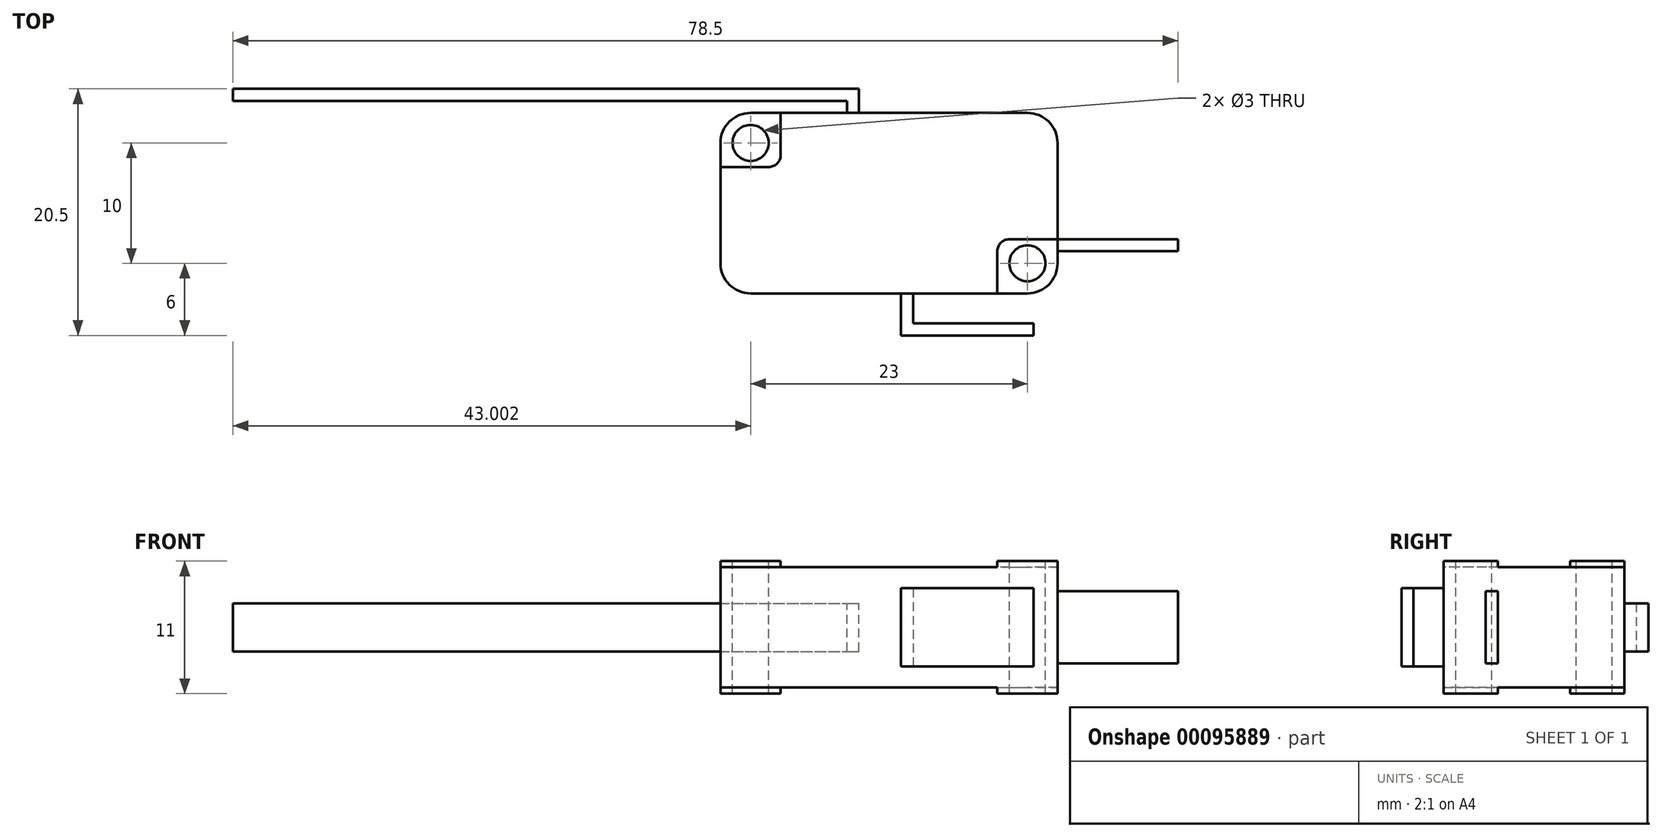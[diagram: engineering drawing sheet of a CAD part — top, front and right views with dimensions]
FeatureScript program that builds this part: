
annotation { "Feature Type Name" : "Feature", "Feature Type Description" : "" }
export const myFeature = defineFeature(function(context is Context, id is Id, definition is map)
    precondition{}
    {
        {
            var Q0;
            Q0=qCreatedBy(makeId("Top.planeOp"),FACE);
            var sketch = newSketch(context, id + "F0", { "sketchPlane" : qUnion([Q0])});
            skLineSegment(sketch, "E0.bottom", {"start": v(-11.85, 4.57) * mm, "end": v(11.15, 4.57) * mm});
            skLineSegment(sketch, "E0.top", {"start": v(-11.85, -10.43) * mm, "end": v(11.15, -10.43) * mm});
            skLineSegment(sketch, "E0.left", {"start": v(-14.35, 2.07) * mm, "end": v(-14.35, -7.93) * mm});
            skLineSegment(sketch, "E0.right", {"start": v(13.65, 2.07) * mm, "end": v(13.65, -7.93) * mm});
            skPoint(sketch, "E1.visualSharp", {"position": v(-14.35, 4.57) * mm});
            skArc(sketch, "E1.filletArc", {"start": v(-11.85, 4.57) * mm, "mid": v(-13.62, 3.84) * mm, "end": v(-14.35, 2.07) * mm});
            skPoint(sketch, "E2.visualSharp", {"position": v(13.65, 4.57) * mm});
            skArc(sketch, "E2.filletArc", {"start": v(13.65, 2.07) * mm, "mid": v(12.92, 3.84) * mm, "end": v(11.15, 4.57) * mm});
            skPoint(sketch, "E3.visualSharp", {"position": v(13.65, -10.43) * mm});
            skArc(sketch, "E3.filletArc", {"start": v(11.15, -10.43) * mm, "mid": v(12.92, -9.7) * mm, "end": v(13.65, -7.93) * mm});
            skPoint(sketch, "E4.visualSharp", {"position": v(-14.35, -10.43) * mm});
            skArc(sketch, "E4.filletArc", {"start": v(-14.35, -7.93) * mm, "mid": v(-13.62, -9.7) * mm, "end": v(-11.85, -10.43) * mm});
            skSolve(sketch);
        }
        {
            var Q0;
            Q0=qSketchRegion(id+"F0",true);
            extrude(context, id + "F1", {"entities" : qUnion([Q0]), "depth" : 10 * mm});
        }
        {
            var Q0;
            Q0=makeQuery(id+"F1.opExtrude","CAP_FACE",FACE,{"disambiguationData":[OSD([sQuery(id+"F0.wireOp",EDGE,"E0.bottom"),sQuery(id+"F0.wireOp",EDGE,"E0.top"),sQuery(id+"F0.wireOp",EDGE,"E0.left"),sQuery(id+"F0.wireOp",EDGE,"E0.right"),sQuery(id+"F0.wireOp",EDGE,"E1.filletArc"),sQuery(id+"F0.wireOp",EDGE,"E2.filletArc"),sQuery(id+"F0.wireOp",EDGE,"E3.filletArc"),sQuery(id+"F0.wireOp",EDGE,"E4.filletArc")])],"isStart":false});
            var sketch = newSketch(context, id + "F2", { "sketchPlane" : qUnion([Q0])});
            skCircle(sketch, "E5", {"center": v(-11.85, 2.07) * mm, "radius": 1.5 * mm});
            skCircle(sketch, "E6", {"center": v(11.15, -7.93) * mm, "radius": 1.5 * mm});
            skSolve(sketch);
        }
        {
            var Q0;
            Q0=qSketchRegion(id+"F2",true);
            extrude(context, id + "F3", {"entities" : qUnion([Q0]), "operationType" : NewBodyOperationType.REMOVE, "oppositeDirection" : true, "depth" : 15 * mm});
        }
        {
            var Q0;
            Q0=makeQuery(id+"F1.opExtrude","CAP_FACE",FACE,{"disambiguationData":[OSD([sQuery(id+"F0.wireOp",EDGE,"E0.bottom"),sQuery(id+"F0.wireOp",EDGE,"E0.top"),sQuery(id+"F0.wireOp",EDGE,"E0.left"),sQuery(id+"F0.wireOp",EDGE,"E0.right"),sQuery(id+"F0.wireOp",EDGE,"E1.filletArc"),sQuery(id+"F0.wireOp",EDGE,"E2.filletArc"),sQuery(id+"F0.wireOp",EDGE,"E3.filletArc"),sQuery(id+"F0.wireOp",EDGE,"E4.filletArc")])],"isStart":false});
            var sketch = newSketch(context, id + "F4", { "sketchPlane" : qUnion([Q0])});
            skPoint(sketch, "E7", {"position": v(-9.35, 4.57) * mm});
            skPoint(sketch, "E8", {"position": v(-9.35, 0.07) * mm});
            skLineSegment(sketch, "E9.bottom", {"start": v(-9.35, 4.57) * mm, "end": v(-14.35, 4.57) * mm});
            skLineSegment(sketch, "E9.top", {"start": v(-10.35, 0.07) * mm, "end": v(-14.35, 0.07) * mm});
            skLineSegment(sketch, "E9.left", {"start": v(-9.35, 4.57) * mm, "end": v(-9.35, 1.07) * mm});
            skLineSegment(sketch, "E9.right", {"start": v(-14.35, 4.57) * mm, "end": v(-14.35, 0.07) * mm});
            skPoint(sketch, "E10", {"position": v(8.65, -10.43) * mm});
            skPoint(sketch, "E11", {"position": v(8.65, -5.93) * mm});
            skLineSegment(sketch, "E12.bottom", {"start": v(9.65, -5.93) * mm, "end": v(13.66, -5.93) * mm});
            skLineSegment(sketch, "E12.top", {"start": v(8.65, -10.43) * mm, "end": v(13.66, -10.43) * mm});
            skLineSegment(sketch, "E12.left", {"start": v(8.65, -6.93) * mm, "end": v(8.65, -10.43) * mm});
            skLineSegment(sketch, "E12.right", {"start": v(13.66, -5.93) * mm, "end": v(13.66, -10.43) * mm});
            skArc(sketch, "E13.filletArc", {"start": v(9.65, -5.93) * mm, "mid": v(8.95, -6.22) * mm, "end": v(8.65, -6.93) * mm});
            skArc(sketch, "E14.filletArc", {"start": v(-10.35, 0.07) * mm, "mid": v(-9.64, 0.36) * mm, "end": v(-9.35, 1.07) * mm});
            skSolve(sketch);
        }
        {
            var Q0;
            {var subQ3=sQuery(id+"F4.wireOp",EDGE,"E9.top");Q0=makeQuery(id+"F4.imprint","IMPRINT",FACE,{"disambiguationData":[TD([[makeQuery(id+"F4.imprint","IMPRINT",EDGE,{"derivedFrom":subQ3}),-1.0]])]});}
            var Q1;
            {var subQ3=sQuery(id+"F4.wireOp",EDGE,"E12.left");Q1=makeQuery(id+"F4.imprint","IMPRINT",FACE,{"disambiguationData":[TD([[makeQuery(id+"F4.imprint","IMPRINT",EDGE,{"derivedFrom":subQ3}),1.0]])]});}
            extrude(context, id + "F5", {"entities" : qUnion([Q0, Q1]), "operationType" : NewBodyOperationType.ADD, "depth" : 0.5 * mm});
        }
        {
            var Q0;
            Q0=makeQuery(id+"F1.opExtrude","CAP_FACE",FACE,{"disambiguationData":[OSD([sQuery(id+"F0.wireOp",EDGE,"E0.bottom"),sQuery(id+"F0.wireOp",EDGE,"E0.top"),sQuery(id+"F0.wireOp",EDGE,"E0.left"),sQuery(id+"F0.wireOp",EDGE,"E0.right"),sQuery(id+"F0.wireOp",EDGE,"E1.filletArc"),sQuery(id+"F0.wireOp",EDGE,"E2.filletArc"),sQuery(id+"F0.wireOp",EDGE,"E3.filletArc"),sQuery(id+"F0.wireOp",EDGE,"E4.filletArc")])],"isStart":true});
            var sketch = newSketch(context, id + "F6", { "sketchPlane" : qUnion([Q0])});
            skLineSegment(sketch, "E15.bottom", {"start": v(-14.35, -0.07) * mm, "end": v(-10.35, -0.07) * mm});
            skLineSegment(sketch, "E15.top", {"start": v(-14.35, -4.57) * mm, "end": v(-9.35, -4.57) * mm});
            skLineSegment(sketch, "E15.left", {"start": v(-14.35, -0.07) * mm, "end": v(-14.35, -4.57) * mm});
            skLineSegment(sketch, "E15.right", {"start": v(-9.35, -1.07) * mm, "end": v(-9.35, -4.57) * mm});
            skLineSegment(sketch, "E16.bottom", {"start": v(8.65, 10.43) * mm, "end": v(13.65, 10.43) * mm});
            skLineSegment(sketch, "E16.top", {"start": v(9.65, 5.93) * mm, "end": v(13.65, 5.93) * mm});
            skLineSegment(sketch, "E16.left", {"start": v(8.65, 10.43) * mm, "end": v(8.65, 6.93) * mm});
            skLineSegment(sketch, "E16.right", {"start": v(13.65, 10.43) * mm, "end": v(13.65, 5.93) * mm});
            skPoint(sketch, "E17.visualSharp", {"position": v(8.65, 5.93) * mm});
            skArc(sketch, "E17.filletArc", {"start": v(8.65, 6.93) * mm, "mid": v(8.95, 6.22) * mm, "end": v(9.65, 5.93) * mm});
            skPoint(sketch, "E18.visualSharp", {"position": v(-9.35, -0.07) * mm});
            skArc(sketch, "E18.filletArc", {"start": v(-9.35, -1.07) * mm, "mid": v(-9.64, -0.36) * mm, "end": v(-10.35, -0.07) * mm});
            skSolve(sketch);
        }
        {
            var Q0;
            {var subQ3=sQuery(id+"F6.wireOp",EDGE,"E15.bottom");Q0=makeQuery(id+"F6.imprint","IMPRINT",FACE,{"disambiguationData":[TD([[makeQuery(id+"F6.imprint","IMPRINT",EDGE,{"derivedFrom":subQ3}),-1.0]])]});}
            var Q1;
            {var subQ3=sQuery(id+"F6.wireOp",EDGE,"E16.top");Q1=makeQuery(id+"F6.imprint","IMPRINT",FACE,{"disambiguationData":[TD([[makeQuery(id+"F6.imprint","IMPRINT",EDGE,{"derivedFrom":subQ3}),1.0]])]});}
            extrude(context, id + "F7", {"entities" : qUnion([Q0, Q1]), "operationType" : NewBodyOperationType.ADD, "depth" : 0.5 * mm});
        }
        {
            var Q0;
            {var subQ0=sQuery(id+"F0.wireOp",EDGE,"E0.right");Q0=makeQuery(id+"F7.boolean.opBoolean","MERGE",FACE,{"derivedFrom":[makeQuery(id+"F5.boolean.opBoolean","MERGE",FACE,{"derivedFrom":[makeQuery(id+"F1.opExtrude","SWEPT_FACE",FACE,{"disambiguationData":[OSD([subQ0])]}),makeQuery(id+"F5.opExtrude","SWEPT_FACE",FACE,{"disambiguationData":[OSD([subQ0])]})]}),makeQuery(id+"F7.opExtrude","SWEPT_FACE",FACE,{"disambiguationData":[OSD([sQuery(id+"F6.wireOp",EDGE,"E16.right")])]})]});}
            var sketch = newSketch(context, id + "F8", { "sketchPlane" : qUnion([Q0])});
            skLineSegment(sketch, "E19.bottom", {"start": v(-5.93, 8) * mm, "end": v(-6.93, 8) * mm});
            skLineSegment(sketch, "E19.top", {"start": v(-5.93, 2) * mm, "end": v(-6.93, 2) * mm});
            skLineSegment(sketch, "E19.left", {"start": v(-5.93, 8) * mm, "end": v(-5.93, 2) * mm});
            skLineSegment(sketch, "E19.right", {"start": v(-6.93, 8) * mm, "end": v(-6.93, 2) * mm});
            skSolve(sketch);
        }
        {
            var Q0;
            Q0=makeQuery(id+"F8.imprint","IMPRINT",FACE,{"disambiguationData":[TD([[makeQuery(id+"F8.imprint","IMPRINT",EDGE,{"derivedFrom":sQuery(id+"F8.wireOp",EDGE,"E19.bottom")}),1.0]])]});
            extrude(context, id + "F9", {"entities" : qUnion([Q0]), "operationType" : NewBodyOperationType.ADD, "depth" : 10 * mm});
        }
        {
            var Q0;
            Q0=makeQuery(id+"F7.boolean.opBoolean","MERGE",FACE,{"derivedFrom":[makeQuery(id+"F5.boolean.opBoolean","MERGE",FACE,{"derivedFrom":[makeQuery(id+"F1.opExtrude","SWEPT_FACE",FACE,{"disambiguationData":[OSD([sQuery(id+"F0.wireOp",EDGE,"E0.top")])]}),makeQuery(id+"F5.opExtrude","SWEPT_FACE",FACE,{"disambiguationData":[OSD([sQuery(id+"F4.wireOp",EDGE,"E12.top")])]})]}),makeQuery(id+"F7.opExtrude","SWEPT_FACE",FACE,{"disambiguationData":[OSD([sQuery(id+"F6.wireOp",EDGE,"E16.bottom")])]})]});
            var sketch = newSketch(context, id + "F10", { "sketchPlane" : qUnion([Q0])});
            skLineSegment(sketch, "E20.bottom", {"start": v(0.65, 8.25) * mm, "end": v(1.65, 8.25) * mm});
            skLineSegment(sketch, "E20.top", {"start": v(0.65, 1.75) * mm, "end": v(1.65, 1.75) * mm});
            skLineSegment(sketch, "E20.left", {"start": v(0.65, 8.25) * mm, "end": v(0.65, 1.75) * mm});
            skLineSegment(sketch, "E20.right", {"start": v(1.65, 8.25) * mm, "end": v(1.65, 1.75) * mm});
            skSolve(sketch);
        }
        {
            var Q0;
            Q0=makeQuery(id+"F10.imprint","IMPRINT",FACE,{"disambiguationData":[TD([[makeQuery(id+"F10.imprint","IMPRINT",EDGE,{"derivedFrom":sQuery(id+"F10.wireOp",EDGE,"E20.bottom")}),-1.0]])]});
            extrude(context, id + "F11", {"entities" : qUnion([Q0]), "operationType" : NewBodyOperationType.ADD, "depth" : 3.5 * mm});
        }
        {
            var Q0;
            Q0=makeQuery(id+"F11.opExtrude","SWEPT_FACE",FACE,{"disambiguationData":[OSD([sQuery(id+"F10.wireOp",EDGE,"E20.right")])]});
            var sketch = newSketch(context, id + "F12", { "sketchPlane" : qUnion([Q0])});
            skLineSegment(sketch, "E21.bottom", {"start": v(-13.93, 8.25) * mm, "end": v(-12.93, 8.25) * mm});
            skLineSegment(sketch, "E21.top", {"start": v(-13.93, 1.75) * mm, "end": v(-12.93, 1.75) * mm});
            skLineSegment(sketch, "E21.left", {"start": v(-13.93, 8.25) * mm, "end": v(-13.93, 1.75) * mm});
            skLineSegment(sketch, "E21.right", {"start": v(-12.93, 8.25) * mm, "end": v(-12.93, 1.75) * mm});
            skSolve(sketch);
        }
        {
            var Q0;
            Q0=qSketchRegion(id+"F12",true);
            extrude(context, id + "F13", {"entities" : qUnion([Q0]), "operationType" : NewBodyOperationType.ADD, "depth" : 10 * mm});
        }
        {
            var Q0;
            Q0=makeQuery(id+"F7.boolean.opBoolean","MERGE",FACE,{"derivedFrom":[makeQuery(id+"F5.boolean.opBoolean","MERGE",FACE,{"derivedFrom":[makeQuery(id+"F1.opExtrude","SWEPT_FACE",FACE,{"disambiguationData":[OSD([sQuery(id+"F0.wireOp",EDGE,"E0.bottom")])]}),makeQuery(id+"F5.opExtrude","SWEPT_FACE",FACE,{"disambiguationData":[OSD([sQuery(id+"F4.wireOp",EDGE,"E9.bottom")])]})]}),makeQuery(id+"F7.opExtrude","SWEPT_FACE",FACE,{"disambiguationData":[OSD([sQuery(id+"F6.wireOp",EDGE,"E15.top")])]})]});
            var sketch = newSketch(context, id + "F14", { "sketchPlane" : qUnion([Q0])});
            skLineSegment(sketch, "E22.bottom", {"start": v(3.85, 3) * mm, "end": v(2.85, 3) * mm});
            skLineSegment(sketch, "E22.top", {"start": v(3.85, 7) * mm, "end": v(2.85, 7) * mm});
            skLineSegment(sketch, "E22.left", {"start": v(3.85, 3) * mm, "end": v(3.85, 7) * mm});
            skLineSegment(sketch, "E22.right", {"start": v(2.85, 3) * mm, "end": v(2.85, 7) * mm});
            skSolve(sketch);
        }
        {
            var Q0;
            Q0=qSketchRegion(id+"F14",true);
            extrude(context, id + "F15", {"entities" : qUnion([Q0]), "operationType" : NewBodyOperationType.ADD, "depth" : 2 * mm});
        }
        {
            var Q0;
            Q0=makeQuery(id+"F15.opExtrude","SWEPT_FACE",FACE,{"disambiguationData":[OSD([sQuery(id+"F14.wireOp",EDGE,"E22.left")])]});
            var sketch = newSketch(context, id + "F16", { "sketchPlane" : qUnion([Q0])});
            skLineSegment(sketch, "E23", {"start": v(-5.57, 7) * mm, "end": v(-5.57, 3) * mm});
            skSolve(sketch);
        }
        {
            var Q0;
            Q0=qSketchRegion(id+"F16",true);
            var Q1;
            {var subQ0=sQuery(id+"F16.wireOp",EDGE,"E23");Q1=makeQuery(id+"F16.imprint","IMPRINT",FACE,{"disambiguationData":[TD([[makeQuery(id+"F16.imprint","IMPRINT",EDGE,{"derivedFrom":subQ0}),-1.0]])]});}
            extrude(context, id + "F17", {"entities" : qUnion([Q0, Q1]), "operationType" : NewBodyOperationType.ADD, "depth" : 51 * mm});
        }
    });
